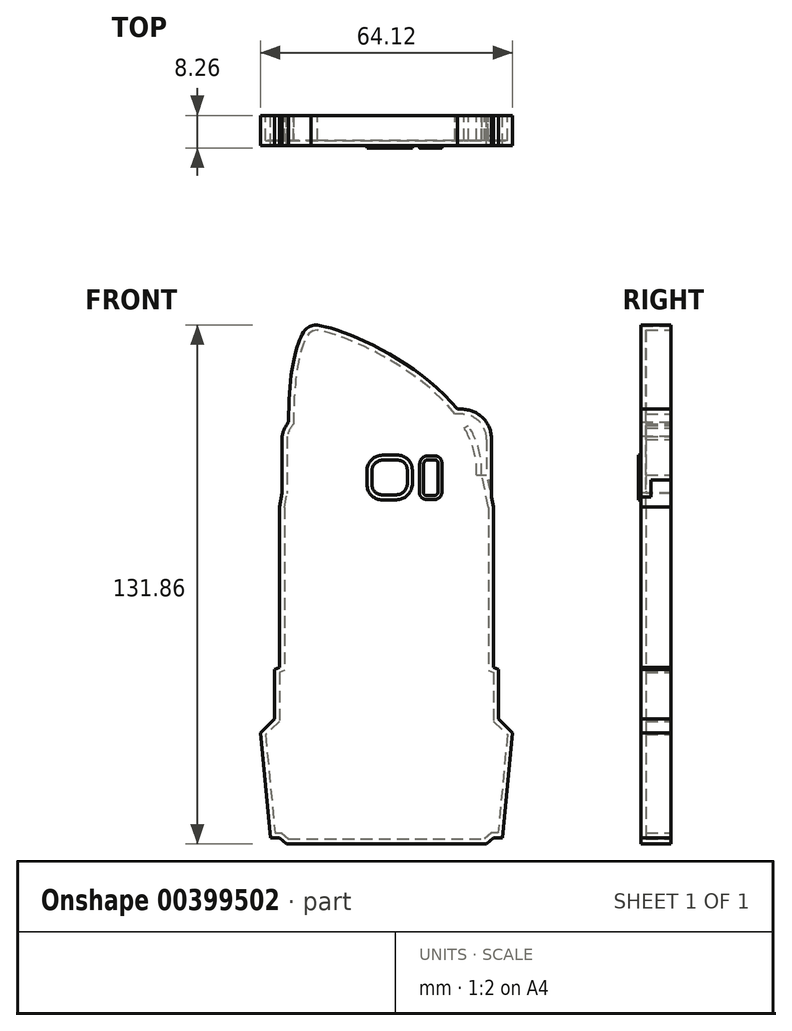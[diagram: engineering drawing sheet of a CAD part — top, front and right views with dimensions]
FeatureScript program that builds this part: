
annotation { "Feature Type Name" : "Feature", "Feature Type Description" : "" }
export const myFeature = defineFeature(function(context is Context, id is Id, definition is map)
    precondition{}
    {
        {
            var Q0;
            Q0=qCreatedBy(makeId("Front.planeOp"),FACE);
            var sketch = newSketch(context, id + "F0", { "sketchPlane" : qUnion([Q0])});
            skLineSegment(sketch, "E0", {"start": v(31.91, 44.57) * mm, "end": v(31.91, 34.16) * mm});
            skLineSegment(sketch, "E1", {"start": v(31.92, 13.5) * mm, "end": v(31.92, -49.87) * mm});
            skLineSegment(sketch, "E2", {"start": v(23.27, -58.16) * mm, "end": v(-12.99, -58.16) * mm});
            skLineSegment(sketch, "E3", {"start": v(-21.1, -49.5) * mm, "end": v(-21.1, 6.28) * mm});
            skLineSegment(sketch, "E4", {"start": v(24.35, 52.21) * mm, "end": v(-12.99, 52.21) * mm});
            skLineSegment(sketch, "E5", {"start": v(-21.27, 45.42) * mm, "end": v(-21.27, 18.78) * mm});
            skArc(sketch, "E6", {"start": v(24.35, 52.21) * mm, "mid": v(29.72, 49.97) * mm, "end": v(31.91, 44.57) * mm});
            skArc(sketch, "E7", {"start": v(-12.99, 52.21) * mm, "mid": v(-18.34, 50.3) * mm, "end": v(-21.27, 45.42) * mm});
            skArc(sketch, "E8", {"start": v(31.92, -49.87) * mm, "mid": v(29.36, -55.86) * mm, "end": v(23.27, -58.16) * mm});
            skArc(sketch, "E9", {"start": v(-12.99, -58.16) * mm, "mid": v(-18.92, -55.6) * mm, "end": v(-21.1, -49.5) * mm});
            skLineSegment(sketch, "E10", {"start": v(31.91, 34.16) * mm, "end": v(34.2, 34.16) * mm});
            skLineSegment(sketch, "E11.0", {"start": v(34.2, 44.56) * mm, "end": v(34.2, 34.16) * mm});
            skArc(sketch, "E11.1", {"start": v(24.35, 54.5) * mm, "mid": v(31.34, 51.58) * mm, "end": v(34.2, 44.56) * mm});
            skLineSegment(sketch, "E11.2", {"start": v(24.35, 54.5) * mm, "end": v(-12.99, 54.5) * mm});
            skArc(sketch, "E11.3", {"start": v(-12.99, 54.5) * mm, "mid": v(-19.88, 51.99) * mm, "end": v(-23.56, 45.64) * mm});
            skLineSegment(sketch, "E11.4", {"start": v(-23.56, 45.64) * mm, "end": v(-23.56, 18.78) * mm});
            skLineSegment(sketch, "E11.5", {"start": v(-21.27, 18.78) * mm, "end": v(-23.56, 18.78) * mm});
            skLineSegment(sketch, "E11.9", {"start": v(34.73, 24.26) * mm, "end": v(34.71, 24.26) * mm});
            skLineSegment(sketch, "E11.11", {"start": v(34.2, 13.5) * mm, "end": v(34.2, -49.87) * mm});
            skArc(sketch, "E11.12", {"start": v(34.2, -49.87) * mm, "mid": v(30.96, -57.5) * mm, "end": v(23.22, -60.45) * mm});
            skLineSegment(sketch, "E11.13", {"start": v(23.22, -60.45) * mm, "end": v(-12.99, -60.45) * mm});
            skArc(sketch, "E11.14", {"start": v(-12.99, -60.45) * mm, "mid": v(-20.56, -57.18) * mm, "end": v(-23.39, -49.43) * mm});
            skLineSegment(sketch, "E11.15", {"start": v(-23.39, -49.43) * mm, "end": v(-23.39, 6.28) * mm});
            skLineSegment(sketch, "E11.16", {"start": v(-23.39, 6.28) * mm, "end": v(-21.1, 6.28) * mm});
            skPoint(sketch, "E12.start.orphan", {"position": v(32.43, 15.78) * mm});
            skLineSegment(sketch, "E13", {"start": v(34.2, 13.5) * mm, "end": v(31.92, 13.5) * mm});
            skPoint(sketch, "E14.orphan", {"position": v(31.92, 15.78) * mm});
            skLineSegment(sketch, "E15", {"start": v(-23.56, 18.78) * mm, "end": v(-23.39, 6.28) * mm});
            skLineSegment(sketch, "E16", {"start": v(-21.27, 18.78) * mm, "end": v(-21.1, 6.28) * mm});
            skLineSegment(sketch, "E17", {"start": v(34.2, 34.16) * mm, "end": v(34.2, 13.5) * mm});
            skLineSegment(sketch, "E18", {"start": v(31.91, 34.16) * mm, "end": v(31.92, 13.5) * mm});
            skSolve(sketch);
        }
        {
            var Q0;
            Q0=makeQuery(id+"F0.imprint","IMPRINT",FACE,{"disambiguationData":[TD([[makeQuery(id+"F0.imprint","IMPRINT",EDGE,{"derivedFrom":sQuery(id+"F0.wireOp",EDGE,"E0")}),-1.0]])]});
            extrude(context, id + "F1", {"entities" : qUnion([Q0]), "depth" : 7.62 * mm});
        }
        {
            var Q0;
            Q0=makeQuery(id+"F1.opExtrude","CAP_FACE",FACE,{"disambiguationData":[OSD([sQuery(id+"F0.wireOp",EDGE,"E0"),sQuery(id+"F0.wireOp",EDGE,"E1"),sQuery(id+"F0.wireOp",EDGE,"E2"),sQuery(id+"F0.wireOp",EDGE,"E3"),sQuery(id+"F0.wireOp",EDGE,"E4"),sQuery(id+"F0.wireOp",EDGE,"E5"),sQuery(id+"F0.wireOp",EDGE,"E6"),sQuery(id+"F0.wireOp",EDGE,"E7"),sQuery(id+"F0.wireOp",EDGE,"E8"),sQuery(id+"F0.wireOp",EDGE,"E9"),sQuery(id+"F0.wireOp",EDGE,"bb75414d-56e8-4ebf-947c-b1fa3df4ddbe.0"),sQuery(id+"F0.wireOp",EDGE,"bb75414d-56e8-4ebf-947c-b1fa3df4ddbe.1"),sQuery(id+"F0.wireOp",EDGE,"bb75414d-56e8-4ebf-947c-b1fa3df4ddbe.2"),sQuery(id+"F0.wireOp",EDGE,"bb75414d-56e8-4ebf-947c-b1fa3df4ddbe.3"),sQuery(id+"F0.wireOp",EDGE,"bb75414d-56e8-4ebf-947c-b1fa3df4ddbe.4"),sQuery(id+"F0.wireOp",EDGE,"bb75414d-56e8-4ebf-947c-b1fa3df4ddbe.5"),sQuery(id+"F0.wireOp",EDGE,"bb75414d-56e8-4ebf-947c-b1fa3df4ddbe.6"),sQuery(id+"F0.wireOp",EDGE,"bb75414d-56e8-4ebf-947c-b1fa3df4ddbe.7"),sQuery(id+"F0.wireOp",EDGE,"35a4204d-8211-4e34-a5d2-bb70df10542c.0"),sQuery(id+"F0.wireOp",EDGE,"35a4204d-8211-4e34-a5d2-bb70df10542c.1"),sQuery(id+"F0.wireOp",EDGE,"35a4204d-8211-4e34-a5d2-bb70df10542c.2"),sQuery(id+"F0.wireOp",EDGE,"35a4204d-8211-4e34-a5d2-bb70df10542c.3"),sQuery(id+"F0.wireOp",EDGE,"35a4204d-8211-4e34-a5d2-bb70df10542c.4"),sQuery(id+"F0.wireOp",EDGE,"35a4204d-8211-4e34-a5d2-bb70df10542c.5"),sQuery(id+"F0.wireOp",EDGE,"35a4204d-8211-4e34-a5d2-bb70df10542c.6"),sQuery(id+"F0.wireOp",EDGE,"35a4204d-8211-4e34-a5d2-bb70df10542c.7"),sQuery(id+"F0.wireOp",EDGE,"E16"),sQuery(id+"F0.wireOp",EDGE,"E18")])],"isStart":true});
            shell(context, id + "F2", {"entities" : qUnion([Q0]), "thickness" : 1.27 * mm});
        }
        {
            var Q0;
            Q0=makeQuery(id+"F1.opExtrude","SWEPT_FACE",FACE,{"disambiguationData":[OSD([sQuery(id+"F0.wireOp",EDGE,"E16")])]});
            cPlane(context, id + "F3", {"entities" : qUnion([Q0]), "cplaneType" : CPlaneType.OFFSET, "offset" : 0 * mm, "width" : 152.4 * mm, "height" : 152.4 * mm});
        }
        {
            var Q0;
            Q0=makeQuery(id+"F1.opExtrude","SWEPT_FACE",FACE,{"disambiguationData":[OSD([sQuery(id+"F0.wireOp",EDGE,"E16")])]});
            extrude(context, id + "F4", {"entities" : qUnion([Q0]), "operationType" : NewBodyOperationType.REMOVE, "oppositeDirection" : true, "depth" : 1.27 * mm});
        }
        {
            var Q0;
            Q0=makeQuery(id+"F1.opExtrude","SWEPT_FACE",FACE,{"disambiguationData":[OSD([sQuery(id+"F0.wireOp",EDGE,"E18")])]});
            cPlane(context, id + "F5", {"entities" : qUnion([Q0]), "cplaneType" : CPlaneType.OFFSET, "offset" : 0 * mm, "width" : 152.4 * mm, "height" : 152.4 * mm});
        }
        {
            var Q0;
            Q0=qCreatedBy(id+"F5.planeOp",FACE);
            var sketch = newSketch(context, id + "F6", { "sketchPlane" : qUnion([Q0])});
            skLineSegment(sketch, "E19.bottom", {"start": v(-5.1, 34.2) * mm, "end": v(0, 34.2) * mm});
            skLineSegment(sketch, "E19.top", {"start": v(-5.1, 13.52) * mm, "end": v(0, 13.52) * mm});
            skLineSegment(sketch, "E19.left", {"start": v(-5.1, 34.2) * mm, "end": v(-5.1, 13.52) * mm});
            skLineSegment(sketch, "E19.right", {"start": v(0, 34.2) * mm, "end": v(0, 13.52) * mm});
            skSolve(sketch);
        }
        {
            var Q0;
            Q0=makeQuery(id+"F6.imprint","IMPRINT",FACE,{"disambiguationData":[TD([[makeQuery(id+"F6.imprint","IMPRINT",EDGE,{"derivedFrom":sQuery(id+"F6.wireOp",EDGE,"E19.bottom")}),-1.0]])]});
            extrude(context, id + "F7", {"entities" : qUnion([Q0]), "operationType" : NewBodyOperationType.REMOVE, "oppositeDirection" : true, "depth" : 1.27 * mm});
        }
        {
            var Q0;
            Q0=makeQuery(id+"F1.opExtrude","CAP_FACE",FACE,{"disambiguationData":[OSD([sQuery(id+"F0.wireOp",EDGE,"E0"),sQuery(id+"F0.wireOp",EDGE,"E1"),sQuery(id+"F0.wireOp",EDGE,"E2"),sQuery(id+"F0.wireOp",EDGE,"E3"),sQuery(id+"F0.wireOp",EDGE,"E4"),sQuery(id+"F0.wireOp",EDGE,"E5"),sQuery(id+"F0.wireOp",EDGE,"E6"),sQuery(id+"F0.wireOp",EDGE,"E7"),sQuery(id+"F0.wireOp",EDGE,"E8"),sQuery(id+"F0.wireOp",EDGE,"E9"),sQuery(id+"F0.wireOp",EDGE,"E16"),sQuery(id+"F0.wireOp",EDGE,"E18")])],"isStart":false});
            var sketch = newSketch(context, id + "F8", { "sketchPlane" : qUnion([Q0])});
            skLineSegment(sketch, "E20", {"start": v(8.03, 39.26) * mm, "end": v(4.22, 39.26) * mm});
            skLineSegment(sketch, "E21", {"start": v(7.72, 30.48) * mm, "end": v(3.9, 30.48) * mm});
            skLineSegment(sketch, "E22", {"start": v(10.5, 36.85) * mm, "end": v(10.5, 33.03) * mm});
            skLineSegment(sketch, "E23", {"start": v(1.56, 36.84) * mm, "end": v(1.56, 33.02) * mm});
            skArc(sketch, "E24", {"start": v(4.22, 39.26) * mm, "mid": v(2.42, 38.56) * mm, "end": v(1.56, 36.84) * mm});
            skArc(sketch, "E25", {"start": v(1.56, 33.02) * mm, "mid": v(2.23, 31.3) * mm, "end": v(3.9, 30.48) * mm});
            skArc(sketch, "E26", {"start": v(7.72, 30.48) * mm, "mid": v(9.6, 31.21) * mm, "end": v(10.5, 33.03) * mm});
            skArc(sketch, "E27", {"start": v(10.5, 36.85) * mm, "mid": v(9.78, 38.57) * mm, "end": v(8.03, 39.26) * mm});
            skArc(sketch, "E28.0", {"start": v(4.22, 40.53) * mm, "mid": v(1.54, 39.48) * mm, "end": v(0.29, 36.9) * mm});
            skLineSegment(sketch, "E28.1", {"start": v(8.02, 40.53) * mm, "end": v(4.22, 40.53) * mm});
            skLineSegment(sketch, "E28.2", {"start": v(0.29, 36.9) * mm, "end": v(0.29, 33.02) * mm});
            skArc(sketch, "E28.3", {"start": v(11.77, 36.85) * mm, "mid": v(10.67, 39.48) * mm, "end": v(8.02, 40.53) * mm});
            skArc(sketch, "E28.4", {"start": v(0.29, 33.02) * mm, "mid": v(1.32, 30.41) * mm, "end": v(3.86, 29.2) * mm});
            skLineSegment(sketch, "E28.5", {"start": v(7.72, 29.2) * mm, "end": v(3.86, 29.2) * mm});
            skArc(sketch, "E28.6", {"start": v(7.72, 29.2) * mm, "mid": v(10.49, 30.3) * mm, "end": v(11.77, 32.98) * mm});
            skLineSegment(sketch, "E28.7", {"start": v(11.77, 36.85) * mm, "end": v(11.77, 32.98) * mm});
            skLineSegment(sketch, "E29", {"start": v(14.69, 38.33) * mm, "end": v(14.69, 31.43) * mm});
            skLineSegment(sketch, "E30", {"start": v(18.3, 38.43) * mm, "end": v(18.3, 31.22) * mm});
            skLineSegment(sketch, "E31", {"start": v(15.41, 30.3) * mm, "end": v(17.58, 30.3) * mm});
            skLineSegment(sketch, "E32", {"start": v(15.62, 39.36) * mm, "end": v(17.47, 39.36) * mm});
            skArc(sketch, "E33", {"start": v(14.69, 38.33) * mm, "mid": v(14.96, 39.03) * mm, "end": v(15.62, 39.36) * mm});
            skArc(sketch, "E34", {"start": v(17.47, 39.36) * mm, "mid": v(18.1, 39.08) * mm, "end": v(18.3, 38.43) * mm});
            skArc(sketch, "E35", {"start": v(18.3, 31.22) * mm, "mid": v(18.1, 30.63) * mm, "end": v(17.58, 30.3) * mm});
            skArc(sketch, "E36", {"start": v(15.41, 30.3) * mm, "mid": v(14.74, 30.66) * mm, "end": v(14.69, 31.43) * mm});
            skArc(sketch, "E37.0", {"start": v(13.67, 38.33) * mm, "mid": v(14.22, 39.73) * mm, "end": v(15.57, 40.38) * mm});
            skLineSegment(sketch, "E37.1", {"start": v(15.57, 40.38) * mm, "end": v(17.47, 40.38) * mm});
            skLineSegment(sketch, "E37.2", {"start": v(13.67, 38.33) * mm, "end": v(13.67, 31.6) * mm});
            skArc(sketch, "E37.3", {"start": v(17.47, 40.38) * mm, "mid": v(18.83, 39.79) * mm, "end": v(19.31, 38.39) * mm});
            skArc(sketch, "E37.4", {"start": v(15.41, 29.28) * mm, "mid": v(13.96, 30) * mm, "end": v(13.67, 31.6) * mm});
            skLineSegment(sketch, "E37.5", {"start": v(15.41, 29.28) * mm, "end": v(17.68, 29.28) * mm});
            skArc(sketch, "E37.6", {"start": v(19.31, 31.22) * mm, "mid": v(18.85, 29.95) * mm, "end": v(17.68, 29.28) * mm});
            skLineSegment(sketch, "E37.7", {"start": v(19.31, 38.39) * mm, "end": v(19.31, 31.22) * mm});
            skSolve(sketch);
        }
        {
            var Q0;
            Q0=qSketchRegion(id+"F8",true);
            extrude(context, id + "F9", {"entities" : qUnion([Q0]), "operationType" : NewBodyOperationType.ADD, "endBound" : BoundingType.SYMMETRIC, "oppositeDirection" : true, "depth" : 1.27 * mm});
        }
        {
            var Q0;
            Q0=makeQuery(id+"F9.boolean.opBoolean","SPLIT",FACE,{"disambiguationData":[TD([makeQuery(id+"F9.opExtrude","SWEPT_FACE",FACE,{"disambiguationData":[OSD([sQuery(id+"F8.wireOp",EDGE,"E29")])]})])],"derivedFrom":makeQuery(id+"F1.opExtrude","CAP_FACE",FACE,{"disambiguationData":[OSD([sQuery(id+"F0.wireOp",EDGE,"E0"),sQuery(id+"F0.wireOp",EDGE,"E1"),sQuery(id+"F0.wireOp",EDGE,"E2"),sQuery(id+"F0.wireOp",EDGE,"E3"),sQuery(id+"F0.wireOp",EDGE,"E4"),sQuery(id+"F0.wireOp",EDGE,"E5"),sQuery(id+"F0.wireOp",EDGE,"E6"),sQuery(id+"F0.wireOp",EDGE,"E7"),sQuery(id+"F0.wireOp",EDGE,"E8"),sQuery(id+"F0.wireOp",EDGE,"E9"),sQuery(id+"F0.wireOp",EDGE,"E16"),sQuery(id+"F0.wireOp",EDGE,"E18")])],"isStart":false})});
            var Q1;
            Q1=makeQuery(id+"F9.boolean.opBoolean","SPLIT",FACE,{"disambiguationData":[TD([makeQuery(id+"F9.opExtrude","SWEPT_FACE",FACE,{"disambiguationData":[OSD([sQuery(id+"F8.wireOp",EDGE,"E20")])]})])],"derivedFrom":makeQuery(id+"F1.opExtrude","CAP_FACE",FACE,{"disambiguationData":[OSD([sQuery(id+"F0.wireOp",EDGE,"E0"),sQuery(id+"F0.wireOp",EDGE,"E1"),sQuery(id+"F0.wireOp",EDGE,"E2"),sQuery(id+"F0.wireOp",EDGE,"E3"),sQuery(id+"F0.wireOp",EDGE,"E4"),sQuery(id+"F0.wireOp",EDGE,"E5"),sQuery(id+"F0.wireOp",EDGE,"E6"),sQuery(id+"F0.wireOp",EDGE,"E7"),sQuery(id+"F0.wireOp",EDGE,"E8"),sQuery(id+"F0.wireOp",EDGE,"E9"),sQuery(id+"F0.wireOp",EDGE,"E16"),sQuery(id+"F0.wireOp",EDGE,"E18")])],"isStart":false})});
            extrude(context, id + "F10", {"entities" : qUnion([Q0, Q1]), "operationType" : NewBodyOperationType.REMOVE, "oppositeDirection" : true, "depth" : 25.4 * mm});
        }
        {
            var Q0;
            Q0=makeQuery(id+"F1.opExtrude","SWEPT_FACE",FACE,{"disambiguationData":[OSD([sQuery(id+"F0.wireOp",EDGE,"E2")])]});
            cPlane(context, id + "F11", {"entities" : qUnion([Q0]), "cplaneType" : CPlaneType.OFFSET, "offset" : 0 * mm, "width" : 152.4 * mm, "height" : 152.4 * mm});
        }
        {
            var Q0;
            Q0=qCreatedBy(id+"F11.planeOp",FACE);
            var sketch = newSketch(context, id + "F12", { "sketchPlane" : qUnion([Q0])});
            skLineSegment(sketch, "E38.bottom", {"start": v(3.06, 5.59) * mm, "end": v(9.82, 5.59) * mm});
            skLineSegment(sketch, "E38.left", {"start": v(2, 4.58) * mm, "end": v(2, 1.76) * mm});
            skLineSegment(sketch, "E39.bottom", {"start": v(16.78, 5.3) * mm, "end": v(21.78, 5.3) * mm});
            skLineSegment(sketch, "E39.left", {"start": v(15.88, 4.62) * mm, "end": v(15.88, 2.31) * mm});
            skCircle(sketch, "E40", {"center": v(-7.81, 2.67) * mm, "radius": 2.18 * mm});
            skArc(sketch, "E41", {"start": v(2, 4.58) * mm, "mid": v(2.31, 5.3) * mm, "end": v(3.06, 5.59) * mm});
            skPoint(sketch, "E42.orphan", {"position": v(22.32, 1.76) * mm});
            skArc(sketch, "E43", {"start": v(15.88, 4.62) * mm, "mid": v(16.16, 5.18) * mm, "end": v(16.78, 5.3) * mm});
            skLineSegment(sketch, "E44.MirrorCS", {"start": v(21.78, 5.3) * mm, "end": v(16.78, 5.3) * mm});
            skArc(sketch, "E45.MirrorCS", {"start": v(22.68, 4.62) * mm, "mid": v(22.4, 5.18) * mm, "end": v(21.78, 5.3) * mm});
            skLineSegment(sketch, "E46.MirrorCS", {"start": v(22.68, 4.62) * mm, "end": v(22.68, 2.31) * mm});
            skPoint(sketch, "E47.orphan", {"position": v(19.28, 5.3) * mm});
            skLineSegment(sketch, "E48.MirrorCS", {"start": v(16.78, 1.63) * mm, "end": v(21.78, 1.63) * mm});
            skArc(sketch, "E49.MirrorCS", {"start": v(15.88, 2.31) * mm, "mid": v(16.16, 1.75) * mm, "end": v(16.78, 1.63) * mm});
            skLineSegment(sketch, "E50.MirrorCS", {"start": v(15.88, 2.31) * mm, "end": v(15.88, 4.62) * mm});
            skArc(sketch, "E51.MirrorCS", {"start": v(22.68, 2.31) * mm, "mid": v(22.4, 1.75) * mm, "end": v(21.78, 1.63) * mm});
            skLineSegment(sketch, "E52.MirrorCS", {"start": v(22.68, 2.31) * mm, "end": v(22.68, 4.62) * mm});
            skPoint(sketch, "E53.start.orphan", {"position": v(16.78, 1.76) * mm});
            skPoint(sketch, "E54.end.orphan", {"position": v(22.68, 3.47) * mm});
            skPoint(sketch, "E54.start.orphan", {"position": v(15.88, 3.47) * mm});
            skLineSegment(sketch, "E55.MirrorCS", {"start": v(3.06, 0.75) * mm, "end": v(9.82, 0.75) * mm});
            skArc(sketch, "E56.MirrorCS", {"start": v(2, 1.76) * mm, "mid": v(2.31, 1.03) * mm, "end": v(3.06, 0.75) * mm});
            skLineSegment(sketch, "E57.MirrorCS", {"start": v(2, 1.76) * mm, "end": v(2, 4.58) * mm});
            skLineSegment(sketch, "E58.MirrorCS", {"start": v(9.82, 5.59) * mm, "end": v(3.06, 5.59) * mm});
            skArc(sketch, "E59.MirrorCS", {"start": v(10.88, 4.58) * mm, "mid": v(10.57, 5.3) * mm, "end": v(9.82, 5.59) * mm});
            skLineSegment(sketch, "E60.MirrorCS", {"start": v(10.88, 4.58) * mm, "end": v(10.88, 1.76) * mm});
            skArc(sketch, "E61.MirrorCS", {"start": v(10.88, 1.76) * mm, "mid": v(10.57, 1.03) * mm, "end": v(9.82, 0.75) * mm});
            skLineSegment(sketch, "E62.MirrorCS", {"start": v(9.82, 0.75) * mm, "end": v(3.06, 0.75) * mm});
            skPoint(sketch, "E63.orphan", {"position": v(6.44, 5.59) * mm});
            skPoint(sketch, "E64.end.orphan", {"position": v(6.44, 0.82) * mm});
            skPoint(sketch, "E65.start.orphan", {"position": v(2, 3.17) * mm});
            skSolve(sketch);
        }
        {
            var Q0;
            Q0=makeQuery(id+"F12.imprint","IMPRINT",FACE,{"disambiguationData":[TD([[makeQuery(id+"F12.imprint","IMPRINT",EDGE,{"derivedFrom":sQuery(id+"F12.wireOp",EDGE,"E40")}),1.0]])]});
            var Q1;
            Q1=makeQuery(id+"F12.imprint","IMPRINT",FACE,{"disambiguationData":[TD([[makeQuery(id+"F12.imprint","IMPRINT",EDGE,{"derivedFrom":sQuery(id+"F12.wireOp",EDGE,"E41")}),-1.0]])]});
            var Q2;
            Q2=makeQuery(id+"F12.imprint","IMPRINT",FACE,{"disambiguationData":[TD([[makeQuery(id+"F12.imprint","IMPRINT",EDGE,{"derivedFrom":sQuery(id+"F12.wireOp",EDGE,"E43")}),-1.0]])]});
            extrude(context, id + "F13", {"entities" : qUnion([Q0, Q1, Q2]), "operationType" : NewBodyOperationType.REMOVE, "oppositeDirection" : true, "depth" : 1.27 * mm});
        }
        {
            var Q0;
            Q0=qCreatedBy(makeId("Front.planeOp"),FACE);
            cPlane(context, id + "F14", {"entities" : qUnion([Q0]), "cplaneType" : CPlaneType.OFFSET, "offset" : 0 * mm, "width" : 152.4 * mm, "height" : 152.4 * mm});
        }
        {
            var Q0;
            Q0=qCreatedBy(id+"F14.planeOp",FACE);
            var sketch = newSketch(context, id + "F15", { "sketchPlane" : qUnion([Q0])});
            skLineSegment(sketch, "E66", {"start": v(32.42, 27.4) * mm, "end": v(32.42, -13.33) * mm});
            skLineSegment(sketch, "E67", {"start": v(33.7, -13.84) * mm, "end": v(33.7, -26.52) * mm});
            skLineSegment(sketch, "E68", {"start": v(32.42, -13.33) * mm, "end": v(33.7, -13.84) * mm});
            skLineSegment(sketch, "E69", {"start": v(33.7, -26.52) * mm, "end": v(37.29, -29.98) * mm});
            skLineSegment(sketch, "E70", {"start": v(37.29, -29.98) * mm, "end": v(34.73, -56.74) * mm});
            skLineSegment(sketch, "E71", {"start": v(34.73, -56.74) * mm, "end": v(32.42, -56.74) * mm});
            skLineSegment(sketch, "E72", {"start": v(32.42, -56.74) * mm, "end": v(30.63, -58.27) * mm});
            skLineSegment(sketch, "E73", {"start": v(30.63, -58.27) * mm, "end": v(5.23, -58.27) * mm});
            skLineSegment(sketch, "E74", {"start": v(32.42, 27.4) * mm, "end": v(30.82, 35.48) * mm});
            skLineSegment(sketch, "E75", {"start": v(30.82, 35.48) * mm, "end": v(29.4, 35.48) * mm});
            skLineSegment(sketch, "E76.MirrorCS", {"start": v(-21.97, -56.74) * mm, "end": v(-20.17, -58.27) * mm});
            skLineSegment(sketch, "E77.MirrorCS", {"start": v(-24.27, -56.74) * mm, "end": v(-21.97, -56.74) * mm});
            skLineSegment(sketch, "E78.MirrorCS", {"start": v(-23.25, -26.52) * mm, "end": v(-26.83, -29.98) * mm});
            skLineSegment(sketch, "E79.MirrorCS", {"start": v(-21.97, 27.4) * mm, "end": v(-20.36, 35.48) * mm});
            skLineSegment(sketch, "E80.MirrorCS", {"start": v(-21.97, -13.33) * mm, "end": v(-23.25, -13.84) * mm});
            skLineSegment(sketch, "E81.MirrorCS", {"start": v(-20.36, 35.48) * mm, "end": v(-18.94, 35.48) * mm});
            skLineSegment(sketch, "E82.MirrorCS", {"start": v(-26.83, -29.98) * mm, "end": v(-24.27, -56.74) * mm});
            skLineSegment(sketch, "E83.MirrorCS", {"start": v(-21.97, 27.4) * mm, "end": v(-21.97, -13.33) * mm});
            skLineSegment(sketch, "E84.MirrorCS", {"start": v(-23.25, -13.84) * mm, "end": v(-23.25, -26.52) * mm});
            skLineSegment(sketch, "E85.MirrorCS", {"start": v(-20.17, -58.27) * mm, "end": v(5.23, -58.27) * mm});
            skFitSpline(sketch, "E86", {"points": [v(29.4, 35.48) * mm, v(-13.9, 73.3) * mm], "startDerivative": vector(3.46, 72.96) * mm, "endDerivative": vector(-5.52, -7.98) * mm});
            skFitSpline(sketch, "E87", {"points": [v(-13.9, 73.3) * mm, v(-18.94, 35.48) * mm], "startDerivative": vector(-11.56, -2.02) * mm, "endDerivative": vector(6.6, -68.81) * mm});
            skFitSpline(sketch, "E88", {"points": [v(-13.9, 73.3) * mm, v(26.06, 48.1) * mm], "startDerivative": vector(-33.72, -22.24) * mm, "endDerivative": vector(12.54, 55.46) * mm});
            skLineSegment(sketch, "E89", {"start": v(-21.97, -13.33) * mm, "end": v(32.42, -13.33) * mm});
            skLineSegment(sketch, "E90", {"start": v(-23.25, -26.52) * mm, "end": v(33.7, -26.52) * mm});
            skSolve(sketch);
        }
        {
            var Q0;
            Q0 = qSketchRegion(id + "F15", true);
            extrude(context, id + "F16", {"entities" : qUnion([Q0]), "operationType" : NewBodyOperationType.ADD, "depth" : 7.62 * mm});
        }
        {
            var Q0;
            {var subQ0=sQuery(id+"F15.wireOp",EDGE,"E86");var subQ9=sQuery(id+"F0.wireOp",EDGE,"E4");Q0=makeQuery(id+"F16.boolean.opBoolean","SPLIT",FACE,{"disambiguationData":[TD([makeQuery(id+"F2.opShell","OFFSET_FACE",FACE,{"disambiguationData":[OSD([subQ9])]})])],"derivedFrom":makeQuery(id+"F16.opExtrude","SWEPT_FACE",FACE,{"disambiguationData":[OSD([subQ0])]})});}
            var Q1;
            {var subQ0=sQuery(id+"F0.wireOp",EDGE,"E7");var subQ12=sQuery(id+"F15.wireOp",EDGE,"E87");Q1=makeQuery(id+"F16.boolean.opBoolean","SPLIT",FACE,{"disambiguationData":[TD([makeQuery(id+"F2.opShell","OFFSET_FACE",FACE,{"disambiguationData":[OSD([subQ0])]})])],"derivedFrom":makeQuery(id+"F16.opExtrude","SWEPT_FACE",FACE,{"disambiguationData":[OSD([subQ12])]})});}
            var Q2;
            Q2=makeQuery(id+"F16.opExtrude","SWEPT_FACE",FACE,{"disambiguationData":[OSD([sQuery(id+"F15.wireOp",EDGE,"E81.MirrorCS")])]});
            var Q3;
            {var subQ0=sQuery(id+"F0.wireOp",EDGE,"E7");var subQ1=sQuery(id+"F0.wireOp",EDGE,"E5");var subQ2=sQuery(id+"F0.wireOp",EDGE,"E0");var subQ3=sQuery(id+"F0.wireOp",EDGE,"E16");var subQ4=sQuery(id+"F0.wireOp",EDGE,"E4");var subQ5=sQuery(id+"F0.wireOp",EDGE,"E6");var subQ6=sQuery(id+"F0.wireOp",EDGE,"E18");var subQ7=sQuery(id+"F0.wireOp",EDGE,"E9");var subQ8=sQuery(id+"F0.wireOp",EDGE,"E8");var subQ9=sQuery(id+"F0.wireOp",EDGE,"E3");var subQ10=sQuery(id+"F0.wireOp",EDGE,"E2");var subQ11=sQuery(id+"F0.wireOp",EDGE,"E1");var subQ12=makeQuery(id+"F1.opExtrude","CAP_FACE",FACE,{"disambiguationData":[OSD([subQ2,subQ11,subQ10,subQ9,subQ4,subQ1,subQ5,subQ0,subQ8,subQ7,subQ3,subQ6])],"isStart":true});Q3=makeQuery(id+"F16.boolean.opBoolean","MERGE",FACE,{"derivedFrom":[makeQuery(id+"F7.boolean.opBoolean","SPLIT",FACE,{"disambiguationData":[TD([makeQuery(id+"F1.opExtrude","SWEPT_FACE",FACE,{"disambiguationData":[OSD([subQ11])]})])],"derivedFrom":subQ12}),makeQuery(id+"F7.boolean.opBoolean","SPLIT",FACE,{"disambiguationData":[TD([makeQuery(id+"F1.opExtrude","SWEPT_FACE",FACE,{"disambiguationData":[OSD([subQ2])]})])],"derivedFrom":subQ12}),makeQuery(id+"F16.opExtrude","CAP_FACE",FACE,{"disambiguationData":[OSD([sQuery(id+"F15.wireOp",EDGE,"E66"),sQuery(id+"F15.wireOp",EDGE,"E67"),sQuery(id+"F15.wireOp",EDGE,"E68"),sQuery(id+"F15.wireOp",EDGE,"E69"),sQuery(id+"F15.wireOp",EDGE,"E70"),sQuery(id+"F15.wireOp",EDGE,"E71"),sQuery(id+"F15.wireOp",EDGE,"E72"),sQuery(id+"F15.wireOp",EDGE,"E73"),sQuery(id+"F15.wireOp",EDGE,"E74"),sQuery(id+"F15.wireOp",EDGE,"E75"),sQuery(id+"F15.wireOp",EDGE,"E76.MirrorCS"),sQuery(id+"F15.wireOp",EDGE,"E77.MirrorCS"),sQuery(id+"F15.wireOp",EDGE,"E78.MirrorCS"),sQuery(id+"F15.wireOp",EDGE,"E79.MirrorCS"),sQuery(id+"F15.wireOp",EDGE,"E80.MirrorCS"),sQuery(id+"F15.wireOp",EDGE,"E81.MirrorCS"),sQuery(id+"F15.wireOp",EDGE,"E82.MirrorCS"),sQuery(id+"F15.wireOp",EDGE,"E83.MirrorCS"),sQuery(id+"F15.wireOp",EDGE,"E84.MirrorCS"),sQuery(id+"F15.wireOp",EDGE,"E85.MirrorCS"),sQuery(id+"F15.wireOp",EDGE,"E86"),sQuery(id+"F15.wireOp",EDGE,"E87")])],"isStart":true})]});}
            var Q4;
            Q4=makeQuery(id+"F16.opExtrude","SWEPT_FACE",FACE,{"disambiguationData":[OSD([sQuery(id+"F15.wireOp",EDGE,"E75")])]});
            shell(context, id + "F17", {"entities" : qUnion([Q0, Q1, Q2, Q3, Q4]), "thickness" : 1.27 * mm});
        }
    });
